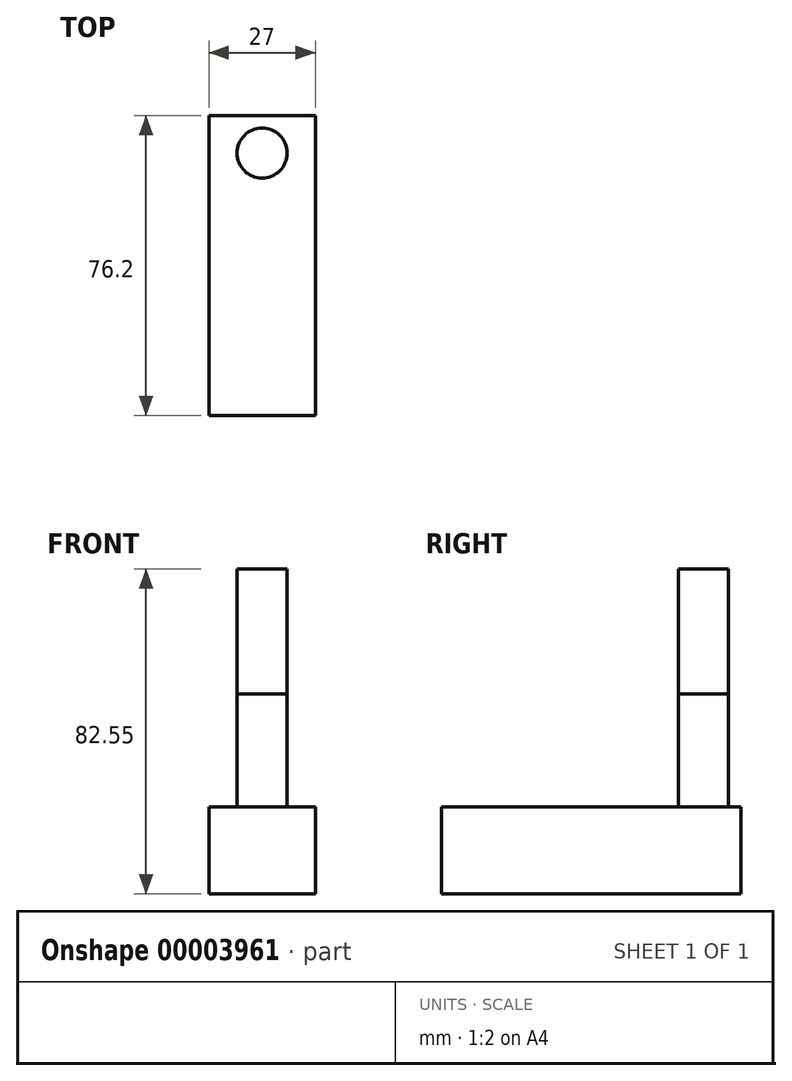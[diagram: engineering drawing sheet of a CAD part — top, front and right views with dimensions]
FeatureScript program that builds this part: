
annotation { "Feature Type Name" : "Feature", "Feature Type Description" : "" }
export const myFeature = defineFeature(function(context is Context, id is Id, definition is map)
    precondition{}
    {
        {
            var Q0;
            Q0=qCreatedBy(makeId("Right.planeOp"),FACE);
            var sketch = newSketch(context, id + "F0", { "sketchPlane" : qUnion([Q0])});
            skLineSegment(sketch, "E0", {"start": v(-56.34, 0) * mm, "end": v(53.63, 0) * mm, "construction": true});
            skLineSegment(sketch, "E1", {"start": v(0, 59.05) * mm, "end": v(0, -62.01) * mm, "construction": true});
            skLineSegment(sketch, "E2.0", {"start": v(-38.1, 0) * mm, "end": v(-38.1, -50.8) * mm});
            skLineSegment(sketch, "E3.0", {"start": v(-38.1, -50.8) * mm, "end": v(0, -50.8) * mm});
            skLineSegment(sketch, "E4.0.MirrorCS", {"start": v(38.1, 0) * mm, "end": v(38.1, -50.8) * mm});
            skLineSegment(sketch, "E5.0.MirrorCS", {"start": v(38.1, -50.8) * mm, "end": v(0, -50.8) * mm});
            skLineSegment(sketch, "E6", {"start": v(-38.1, 0) * mm, "end": v(38.1, 0) * mm});
            skSolve(sketch);
        }
        {
            var Q0;
            Q0 = qSketchRegion(id + "F0", true);
            extrude(context, id + "F1", {"entities" : qUnion([Q0]), "endBound" : BoundingType.SYMMETRIC, "depth" : 27 * mm});
        }
        {
            var Q0;
            Q0=qCreatedBy(makeId("Right.planeOp"),FACE);
            var sketch = newSketch(context, id + "F2", { "sketchPlane" : qUnion([Q0])});
            skLineSegment(sketch, "E7.0.0", {"start": v(-38.1, 0) * mm, "end": v(38.1, 0) * mm});
            skLineSegment(sketch, "E8.top", {"start": v(-38.1, 31.75) * mm, "end": v(38.1, 31.75) * mm});
            skLineSegment(sketch, "E8.left", {"start": v(-38.1, 0) * mm, "end": v(-38.1, 31.75) * mm});
            skLineSegment(sketch, "E8.right", {"start": v(38.1, 0) * mm, "end": v(38.1, 31.75) * mm});
            skSolve(sketch);
        }
        {
            var Q0;
            Q0=makeQuery(id+"F2.imprint","IMPRINT",FACE,{"disambiguationData":[TD([[makeQuery(id+"F2.imprint","IMPRINT",EDGE,{"derivedFrom":sQuery(id+"F2.wireOp",EDGE,"E7.0.0")}),1.0]])]});
            extrude(context, id + "F3", {"entities" : qUnion([Q0]), "endBound" : BoundingType.SYMMETRIC, "depth" : 27 * mm});
        }
        {
            var Q0;
            Q0=makeQuery(id+"F1.opExtrude","CAP_FACE",FACE,{"disambiguationData":[OSD([sQuery(id+"F0.wireOp",EDGE,"E2.0"),sQuery(id+"F0.wireOp",EDGE,"E3.0"),sQuery(id+"F0.wireOp",EDGE,"E4.0.MirrorCS"),sQuery(id+"F0.wireOp",EDGE,"E6")])],"isStart":true});
            var sketch = newSketch(context, id + "F4", { "sketchPlane" : qUnion([Q0])});
            skCircle(sketch, "E9", {"center": v(0, 0) * mm, "radius": 25.6 * mm});
            skSolve(sketch);
        }
        {
            var Q0;
            {var subQ0=makeQuery(id+"F1.opExtrude","CAP_EDGE",EDGE,{"disambiguationData":[OSD([sQuery(id+"F0.wireOp",EDGE,"E6")])],"isStart":true});var subQ1=sQuery(id+"F4.wireOp",EDGE,"E9");var subQ3=makeQuery(id+"F4.imprint","INTERSECT",VERTEX,{"disambiguationData":[OD(0.0)],"derivedFrom":[subQ0,subQ1]});Q0=qUnion([makeQuery(id+"F4.imprint","IMPRINT",FACE,{"disambiguationData":[TD([[makeQuery(id+"F4.imprint","IMPRINT",EDGE,{"disambiguationData":[TD([[subQ3,-1.0]])],"derivedFrom":subQ1}),1.0]])]}),makeQuery(id+"F4.imprint","IMPRINT",FACE,{"disambiguationData":[TD([[makeQuery(id+"F4.imprint","IMPRINT",EDGE,{"disambiguationData":[TD([[subQ3,1.0]])],"derivedFrom":subQ1}),1.0]])]})]);}
            extrude(context, id + "F5", {"entities" : qUnion([Q0]), "operationType" : NewBodyOperationType.REMOVE, "oppositeDirection" : true, "depth" : 1.6 * mm});
        }
        {
            var Q0;
            {var subQ0=sQuery(id+"F4.wireOp",EDGE,"E9");Q0=makeQuery(id+"F5.boolean.opBoolean","COPY",FACE,{"disambiguationData":[TD([makeQuery(id+"F3.opExtrude","SWEPT_FACE",FACE,{"disambiguationData":[OSD([sQuery(id+"F2.wireOp",EDGE,"E7.0.0")])]})])],"derivedFrom":makeQuery(id+"F5.opExtrude","CAP_FACE",FACE,{"disambiguationData":[OSD([subQ0])],"isStart":false})});}
            var sketch = newSketch(context, id + "F6", { "sketchPlane" : qUnion([Q0])});
            skCircle(sketch, "E10", {"center": v(0, 0) * mm, "radius": 19.05 * mm});
            skSolve(sketch);
        }
        {
            var Q0;
            {var subQ0=sQuery(id+"F6.wireOp",EDGE,"E10");var subQ1=makeQuery(id+"F5.boolean.opBoolean","INTERSECT",EDGE,{"derivedFrom":[makeQuery(id+"F3.opExtrude","SWEPT_FACE",FACE,{"disambiguationData":[OSD([sQuery(id+"F2.wireOp",EDGE,"E7.0.0")])]}),makeQuery(id+"F5.opExtrude","CAP_FACE",FACE,{"disambiguationData":[OSD([sQuery(id+"F4.wireOp",EDGE,"E9")])],"isStart":false})]});var subQ2=makeQuery(id+"F6.imprint","INTERSECT",VERTEX,{"disambiguationData":[OD(0.0)],"derivedFrom":[subQ1,subQ0]});Q0=qUnion([makeQuery(id+"F6.imprint","IMPRINT",FACE,{"disambiguationData":[TD([[makeQuery(id+"F6.imprint","IMPRINT",EDGE,{"disambiguationData":[TD([[subQ2,1.0]])],"derivedFrom":subQ0}),1.0]])]}),makeQuery(id+"F6.imprint","IMPRINT",FACE,{"disambiguationData":[TD([[makeQuery(id+"F6.imprint","IMPRINT",EDGE,{"disambiguationData":[TD([[subQ2,-1.0]])],"derivedFrom":subQ0}),1.0]])]})]);}
            extrude(context, id + "F7", {"entities" : qUnion([Q0]), "operationType" : NewBodyOperationType.REMOVE, "endBound" : BoundingType.THROUGH_ALL, "oppositeDirection" : true, "depth" : 25.4 * mm});
        }
        {
            var Q0;
            Q0=makeQuery(id+"F3.opExtrude","SWEPT_FACE",FACE,{"disambiguationData":[OSD([sQuery(id+"F2.wireOp",EDGE,"E8.top")])]});
            var sketch = newSketch(context, id + "F8", { "sketchPlane" : qUnion([Q0])});
            skLineSegment(sketch, "E11", {"start": v(0, 38.1) * mm, "end": v(0, -38.1) * mm, "construction": true});
            skLineSegment(sketch, "E12", {"start": v(-13.5, 0) * mm, "end": v(13.5, 0) * mm, "construction": true});
            skLineSegment(sketch, "E13.0", {"start": v(-13.5, -28.58) * mm, "end": v(13.5, -28.58) * mm, "construction": true});
            skCircle(sketch, "E14", {"center": v(0, -28.58) * mm, "radius": 6.35 * mm});
            skCircle(sketch, "E15.0.MirrorC", {"center": v(0, 28.58) * mm, "radius": 6.35 * mm});
            skSolve(sketch);
        }
        {
            var Q0;
            Q0=makeQuery(id+"F8.imprint","IMPRINT",FACE,{"disambiguationData":[TD([[makeQuery(id+"F8.imprint","IMPRINT",EDGE,{"derivedFrom":sQuery(id+"F8.wireOp",EDGE,"E15.0.MirrorC")}),-1.0]])]});
            var Q1;
            Q1=makeQuery(id+"F8.imprint","IMPRINT",FACE,{"disambiguationData":[TD([[makeQuery(id+"F8.imprint","IMPRINT",EDGE,{"derivedFrom":sQuery(id+"F8.wireOp",EDGE,"E14")}),1.0]])]});
            extrude(context, id + "F9", {"entities" : qUnion([Q0, Q1]), "operationType" : NewBodyOperationType.REMOVE, "oppositeDirection" : true, "depth" : 60.45 * mm});
        }
    });
